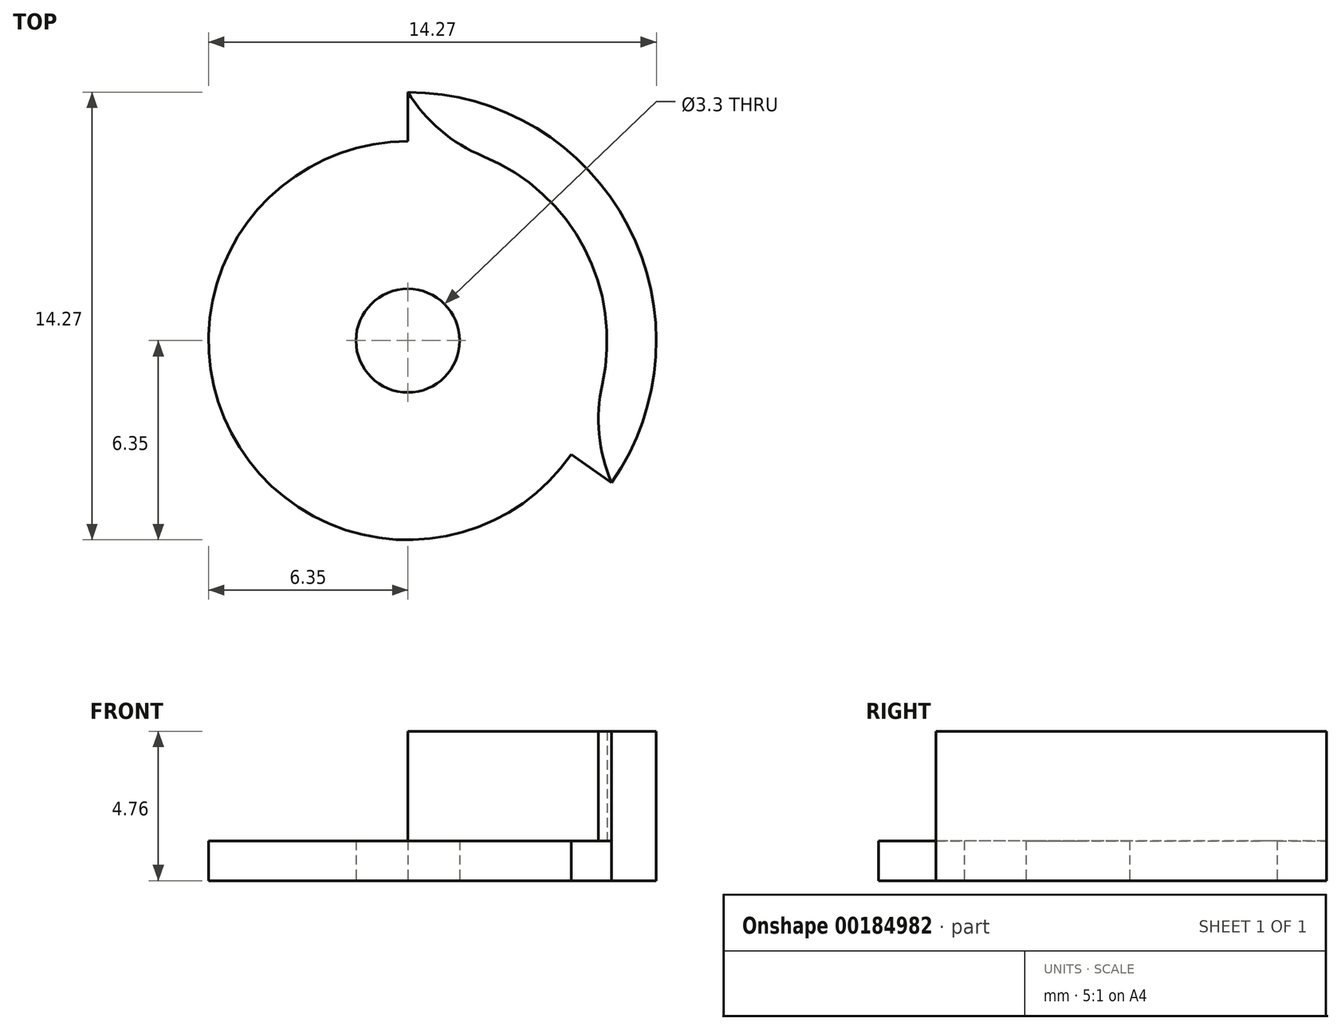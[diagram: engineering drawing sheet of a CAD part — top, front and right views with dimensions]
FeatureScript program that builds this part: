
annotation { "Feature Type Name" : "Feature", "Feature Type Description" : "" }
export const myFeature = defineFeature(function(context is Context, id is Id, definition is map)
    precondition{}
    {
        {
            var Q0;
            Q0=qCreatedBy(makeId("Top.planeOp"),FACE);
            var sketch = newSketch(context, id + "F0", { "sketchPlane" : qUnion([Q0])});
            skCircle(sketch, "E0", {"center": v(0, 0) * mm, "radius": 6.35 * mm});
            skCircle(sketch, "E1", {"center": v(0, 0) * mm, "radius": 1.65 * mm});
            skCircle(sketch, "E2", {"center": v(0, 0) * mm, "radius": 5.16 * mm});
            skPoint(sketch, "E3.start.orphan", {"position": v(5.16, 0) * mm});
            skCircle(sketch, "E4", {"center": v(0, 0) * mm, "radius": 7.92 * mm});
            skLineSegment(sketch, "E5", {"start": v(0, 0) * mm, "end": v(0, 7.92) * mm});
            skLineSegment(sketch, "E6", {"start": v(0, 0) * mm, "end": v(6.5, -4.52) * mm});
            skSolve(sketch);
        }
        {
            var Q0;
            Q0=makeQuery(id+"F0.imprint","IMPRINT",FACE,{"disambiguationData":[TD([[makeQuery(id+"F0.imprint","IMPRINT",EDGE,{"derivedFrom":sQuery(id+"F0.wireOp",EDGE,"E1")}),-1.0]])]});
            var Q1;
            {var subQ0=sQuery(id+"F0.wireOp",EDGE,"CdTnW89r-2r9Z-TSU7-JnKc-Tcu6ddvsWR7h");Q1=makeQuery(id+"F0.imprint","IMPRINT",FACE,{"disambiguationData":[TD([[makeQuery(id+"F0.imprint","IMPRINT",EDGE,{"derivedFrom":subQ0}),1.0]])]});}
            var Q2;
            {var subQ0=sQuery(id+"F0.wireOp",EDGE,"CdTnW89r-2r9Z-TSU7-JnKc-Tcu6ddvsWR7h");Q2=makeQuery(id+"F0.imprint","IMPRINT",FACE,{"disambiguationData":[TD([[makeQuery(id+"F0.imprint","IMPRINT",EDGE,{"derivedFrom":subQ0}),-1.0]])]});}
            var Q3;
            {var subQ0=sQuery(id+"F0.wireOp",EDGE,"yYMdABQl-cBBa-Mjex-pnPG-GefK0XZdQX48");var subQ1=sQuery(id+"F0.wireOp",EDGE,"E0");var subQ2=makeQuery(id+"F0.imprint","INTERSECT",VERTEX,{"derivedFrom":[subQ1,subQ0]});Q3=makeQuery(id+"F0.imprint","IMPRINT",FACE,{"disambiguationData":[TD([[makeQuery(id+"F0.imprint","IMPRINT",EDGE,{"disambiguationData":[TD([[subQ2,1.0]])],"derivedFrom":subQ1}),1.0]])]});}
            var Q4;
            {var subQ0=sQuery(id+"F0.wireOp",EDGE,"gUwOO4lC-ZmBm-NhzQ-4GGR-pJwV4ugRacjK");var subQ1=sQuery(id+"F0.wireOp",EDGE,"E0");var subQ2=makeQuery(id+"F0.imprint","INTERSECT",VERTEX,{"derivedFrom":[subQ1,subQ0]});Q4=makeQuery(id+"F0.imprint","IMPRINT",FACE,{"disambiguationData":[TD([[makeQuery(id+"F0.imprint","IMPRINT",EDGE,{"disambiguationData":[TD([[subQ2,1.0]])],"derivedFrom":subQ1}),1.0]])]});}
            var Q5;
            {var subQ0=sQuery(id+"F0.wireOp",EDGE,"yYMdABQl-cBBa-Mjex-pnPG-GefK0XZdQX48");var subQ1=sQuery(id+"F0.wireOp",EDGE,"E0");var subQ2=makeQuery(id+"F0.imprint","INTERSECT",VERTEX,{"derivedFrom":[subQ1,subQ0]});Q5=makeQuery(id+"F0.imprint","IMPRINT",FACE,{"disambiguationData":[TD([[makeQuery(id+"F0.imprint","IMPRINT",EDGE,{"disambiguationData":[TD([[subQ2,-1.0]])],"derivedFrom":subQ1}),1.0]])]});}
            extrude(context, id + "F1", {"entities" : qUnion([Q0, Q1, Q2, Q3, Q4, Q5]), "depth" : 1.27 * mm});
        }
        {
            var Q0;
            {var subQ0=sQuery(id+"F0.wireOp",EDGE,"E5");var subQ1=sQuery(id+"F0.wireOp",EDGE,"E0");var subQ2=makeQuery(id+"F0.imprint","INTERSECT",VERTEX,{"derivedFrom":[subQ1,subQ0]});Q0=makeQuery(id+"F0.imprint","IMPRINT",FACE,{"disambiguationData":[TD([[makeQuery(id+"F0.imprint","IMPRINT",EDGE,{"disambiguationData":[TD([[subQ2,1.0]])],"derivedFrom":subQ1}),-1.0]])]});}
            extrude(context, id + "F2", {"entities" : qUnion([Q0]), "operationType" : NewBodyOperationType.ADD, "depth" : 4.76 * mm});
        }
        {
            var Q0;
            {var subQ0=sQuery(id+"F0.wireOp",EDGE,"E0");var subQ1=sQuery(id+"F0.wireOp",EDGE,"E5");Q0=makeQuery(id+"F2.boolean.opBoolean","SPLIT",EDGE,{"disambiguationData":[topologyDisambiguationEdgeConnected([makeQuery(id+"F1.opExtrude","SWEPT_FACE",FACE,{"disambiguationData":[OSD([subQ0])]})])],"derivedFrom":makeQuery(id+"F2.opExtrude","SWEPT_EDGE",EDGE,{"disambiguationData":[OSD([subQ0,subQ1])]})});}
            var Q1;
            {var subQ0=sQuery(id+"F0.wireOp",EDGE,"E0");var subQ1=sQuery(id+"F0.wireOp",EDGE,"E6");Q1=makeQuery(id+"F2.boolean.opBoolean","SPLIT",EDGE,{"disambiguationData":[topologyDisambiguationEdgeConnected([makeQuery(id+"F1.opExtrude","SWEPT_FACE",FACE,{"disambiguationData":[OSD([subQ0])]})])],"derivedFrom":makeQuery(id+"F2.opExtrude","SWEPT_EDGE",EDGE,{"disambiguationData":[OSD([subQ0,subQ1])]})});}
            fillet(context, id + "F3", {"entities" : qUnion([Q0, Q1]), "radius" : 5.08 * mm, "tangentPropagation" : true, "allowEdgeOverflow" : false});
        }
    });
